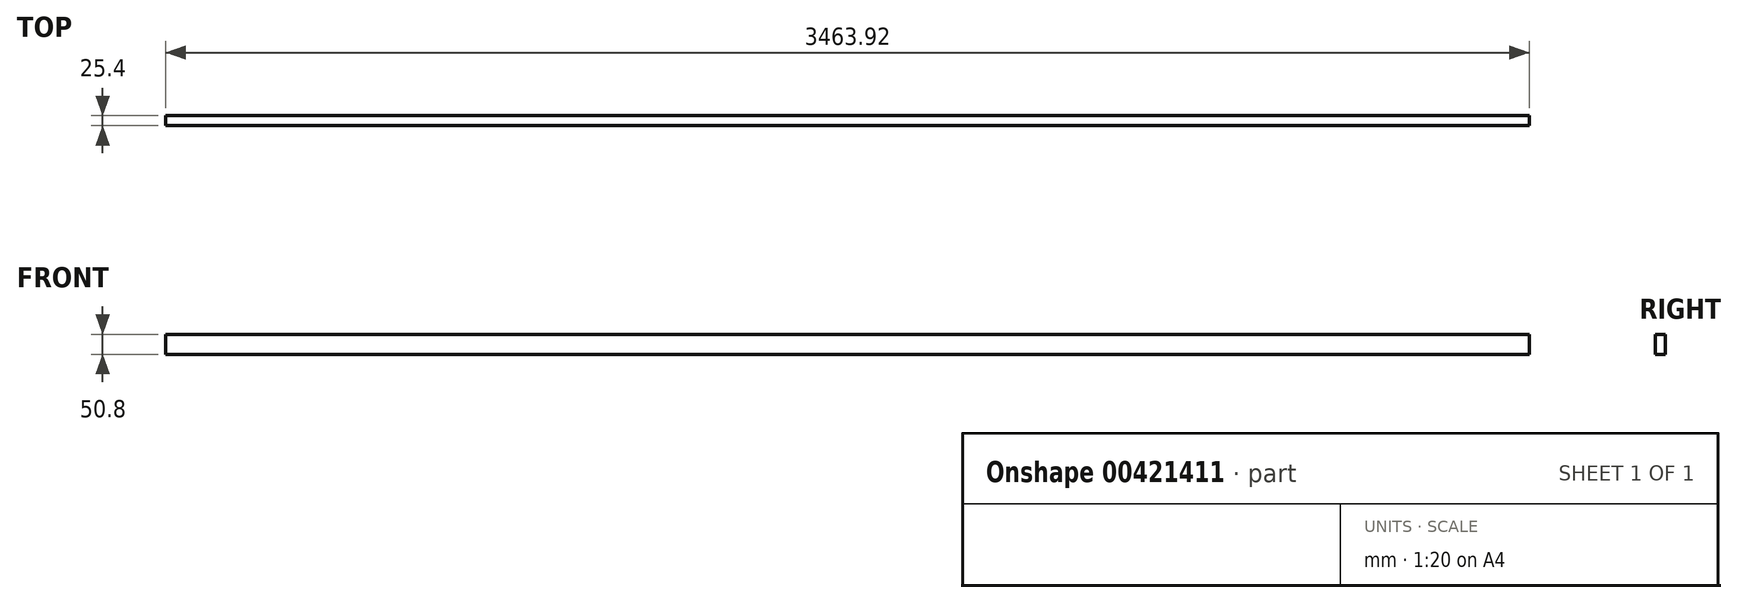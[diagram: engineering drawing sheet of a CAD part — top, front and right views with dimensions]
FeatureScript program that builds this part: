
annotation { "Feature Type Name" : "Feature", "Feature Type Description" : "" }
export const myFeature = defineFeature(function(context is Context, id is Id, definition is map)
    precondition{}
    {
        {
            var Q0;
            Q0=qCreatedBy(makeId("Front.planeOp"),FACE);
            var sketch = newSketch(context, id + "F0", { "sketchPlane" : qUnion([Q0])});
            skLineSegment(sketch, "E0.bottom", {"start": v(1731.96, -25.4) * mm, "end": v(-1731.96, -25.4) * mm});
            skLineSegment(sketch, "E0.top", {"start": v(1731.96, 25.4) * mm, "end": v(-1731.96, 25.4) * mm});
            skLineSegment(sketch, "E0.left", {"start": v(1731.96, -25.4) * mm, "end": v(1731.96, 25.4) * mm});
            skLineSegment(sketch, "E0.right", {"start": v(-1731.96, -25.4) * mm, "end": v(-1731.96, 25.4) * mm});
            skPoint(sketch, "E0.middle", {"position": v(0, 0) * mm});
            skSolve(sketch);
        }
        {
            var Q0;
            Q0 = qSketchRegion(id + "F0", true);
            extrude(context, id + "F1", {"entities" : qUnion([Q0]), "depth" : 25.4 * mm});
        }
    });
